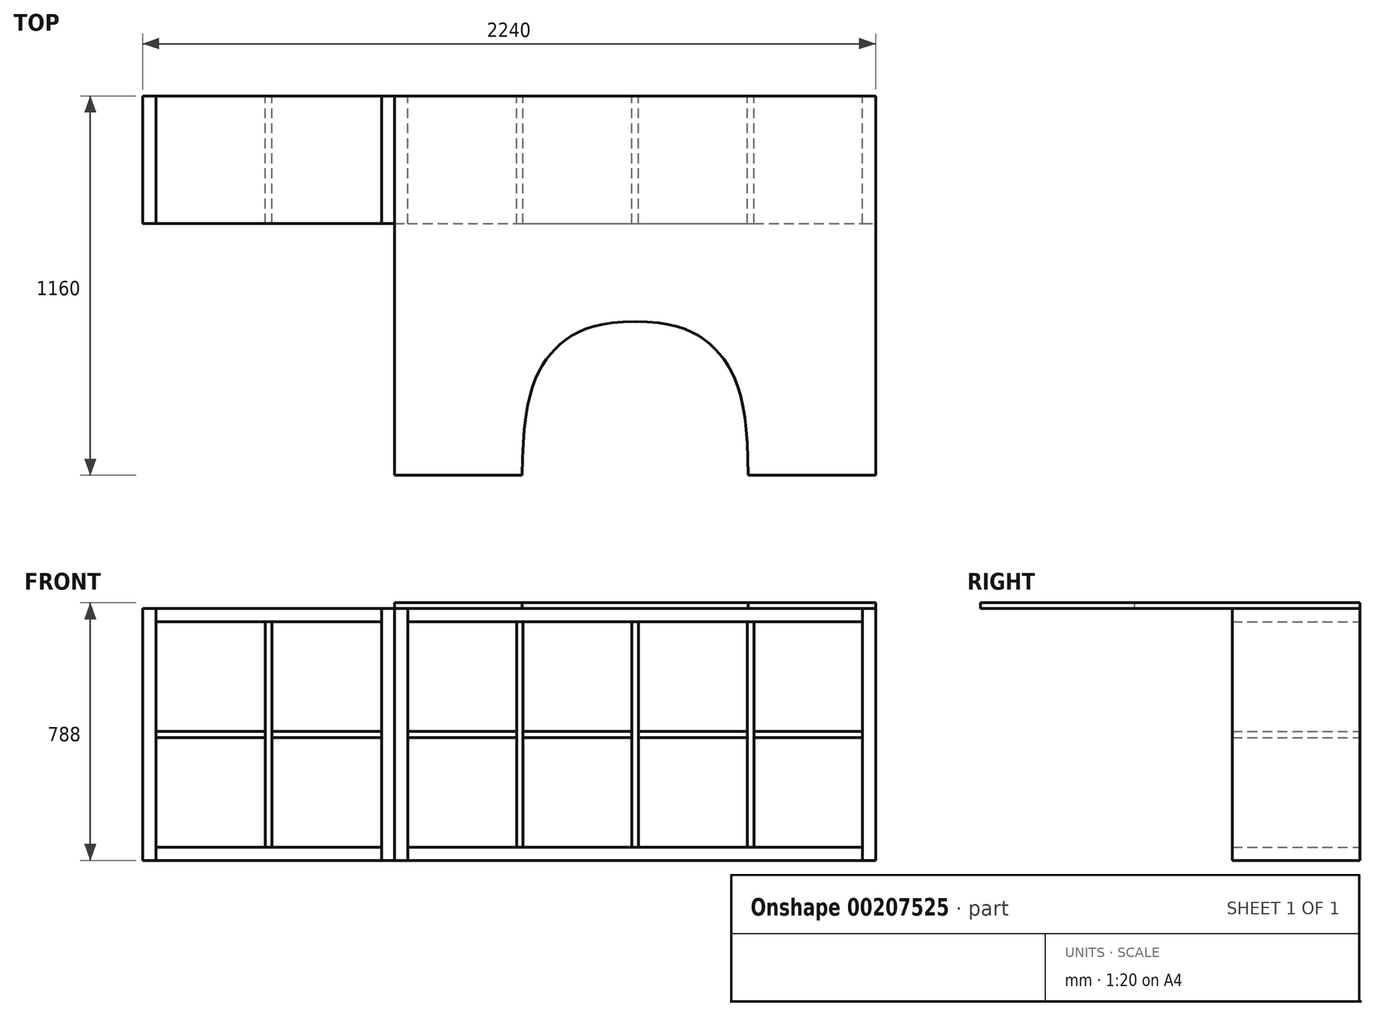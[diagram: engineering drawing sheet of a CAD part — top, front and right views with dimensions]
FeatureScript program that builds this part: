
annotation { "Feature Type Name" : "Feature", "Feature Type Description" : "" }
export const myFeature = defineFeature(function(context is Context, id is Id, definition is map)
    precondition{}
    {
        {
            var Q0;
            Q0=qCreatedBy(makeId("Front.planeOp"),FACE);
            var sketch = newSketch(context, id + "F0", { "sketchPlane" : qUnion([Q0])});
            skLineSegment(sketch, "E0.bottom", {"start": v(0, 0) * mm, "end": v(-770, 0) * mm});
            skLineSegment(sketch, "E0.top", {"start": v(0, 770) * mm, "end": v(-770, 770) * mm});
            skLineSegment(sketch, "E0.left", {"start": v(0, 0) * mm, "end": v(0, 770) * mm});
            skLineSegment(sketch, "E0.right", {"start": v(-770, 0) * mm, "end": v(-770, 770) * mm});
            skLineSegment(sketch, "E1", {"start": v(-770, 385) * mm, "end": v(0, 385) * mm, "construction": true});
            skLineSegment(sketch, "E2", {"start": v(-385, 770) * mm, "end": v(-385, 0) * mm, "construction": true});
            skLineSegment(sketch, "E3", {"start": v(-730, 395) * mm, "end": v(-395, 395) * mm});
            skLineSegment(sketch, "E4", {"start": v(-395, 730) * mm, "end": v(-395, 40) * mm});
            skLineSegment(sketch, "E5.MirrorCS", {"start": v(-375, 730) * mm, "end": v(-375, 40) * mm});
            skLineSegment(sketch, "E6.MirrorCS", {"start": v(-730, 375) * mm, "end": v(-395, 375) * mm});
            skLineSegment(sketch, "E7", {"start": v(-730, 770) * mm, "end": v(-730, 0) * mm});
            skLineSegment(sketch, "E8.MirrorCS", {"start": v(-40, 770) * mm, "end": v(-40, 0) * mm});
            skLineSegment(sketch, "E9", {"start": v(-730, 730) * mm, "end": v(-40, 730) * mm});
            skLineSegment(sketch, "E10.MirrorCS", {"start": v(-730, 40) * mm, "end": v(-40, 40) * mm});
            skPoint(sketch, "E11.orphan", {"position": v(-395, 770) * mm});
            skPoint(sketch, "E12.orphan", {"position": v(-375, 770) * mm});
            skPoint(sketch, "E13.orphan", {"position": v(-770, 395) * mm});
            skPoint(sketch, "E14.orphan", {"position": v(-770, 375) * mm});
            skPoint(sketch, "E15.orphan", {"position": v(0, 395) * mm});
            skPoint(sketch, "E16.orphan", {"position": v(0, 375) * mm});
            skLineSegment(sketch, "E17.trimOffspring", {"start": v(-375, 395) * mm, "end": v(-40, 395) * mm});
            skLineSegment(sketch, "E18.trimOffspring", {"start": v(-375, 375) * mm, "end": v(-40, 375) * mm});
            skPoint(sketch, "E19.orphan", {"position": v(-395, 0) * mm});
            skPoint(sketch, "E20.orphan", {"position": v(-375, 0) * mm});
            skLineSegment(sketch, "E21.bottom", {"start": v(0, 0) * mm, "end": v(1470, 0) * mm});
            skLineSegment(sketch, "E21.top", {"start": v(0, 770) * mm, "end": v(1470, 770) * mm});
            skLineSegment(sketch, "E21.right", {"start": v(1470, 0) * mm, "end": v(1470, 770) * mm});
            skLineSegment(sketch, "E22", {"start": v(0, 385) * mm, "end": v(1470, 385) * mm, "construction": true});
            skLineSegment(sketch, "E23", {"start": v(735, 770) * mm, "end": v(735, 0) * mm, "construction": true});
            skLineSegment(sketch, "E24.bottom", {"start": v(40, 730) * mm, "end": v(1430, 730) * mm});
            skLineSegment(sketch, "E24.top", {"start": v(40, 40) * mm, "end": v(1430, 40) * mm});
            skLineSegment(sketch, "E24.left", {"start": v(40, 770) * mm, "end": v(40, 0) * mm});
            skLineSegment(sketch, "E24.right", {"start": v(1430, 770) * mm, "end": v(1430, 0) * mm});
            skPoint(sketch, "E24.middle", {"position": v(735, 385) * mm});
            skLineSegment(sketch, "E25", {"start": v(725, 730) * mm, "end": v(725, 40) * mm});
            skLineSegment(sketch, "E26", {"start": v(40, 395) * mm, "end": v(372.5, 395) * mm});
            skLineSegment(sketch, "E27.MirrorCS", {"start": v(745, 730) * mm, "end": v(745, 40) * mm});
            skLineSegment(sketch, "E28.MirrorCS", {"start": v(40, 375) * mm, "end": v(372.5, 375) * mm});
            skLineSegment(sketch, "E29", {"start": v(382.5, 730) * mm, "end": v(382.5, 40) * mm, "construction": true});
            skLineSegment(sketch, "E30", {"start": v(372.5, 730) * mm, "end": v(372.5, 40) * mm});
            skLineSegment(sketch, "E31.MirrorCS", {"start": v(392.5, 730) * mm, "end": v(392.5, 40) * mm});
            skLineSegment(sketch, "E32.MirrorCS", {"start": v(1077.5, 730) * mm, "end": v(1077.5, 40) * mm});
            skLineSegment(sketch, "E33.MirrorCS", {"start": v(1097.5, 730) * mm, "end": v(1097.5, 40) * mm});
            skLineSegment(sketch, "E34.trimOffspring", {"start": v(1097.5, 375) * mm, "end": v(1430, 375) * mm});
            skLineSegment(sketch, "E35.trimOffspring", {"start": v(1097.5, 395) * mm, "end": v(1430, 395) * mm});
            skLineSegment(sketch, "E36.trimOffspring", {"start": v(745, 375) * mm, "end": v(1077.5, 375) * mm});
            skLineSegment(sketch, "E37.trimOffspring", {"start": v(745, 395) * mm, "end": v(1077.5, 395) * mm});
            skLineSegment(sketch, "E38.trimOffspring", {"start": v(392.5, 375) * mm, "end": v(725, 375) * mm});
            skLineSegment(sketch, "E39.trimOffspring", {"start": v(392.5, 395) * mm, "end": v(725, 395) * mm});
            skSolve(sketch);
        }
        {
            var Q0;
            {var subQ4=sQuery(id+"F0.wireOp",EDGE,"E0.right");Q0=makeQuery(id+"F0.imprint","IMPRINT",FACE,{"disambiguationData":[TD([[makeQuery(id+"F0.imprint","IMPRINT",EDGE,{"derivedFrom":subQ4}),-1.0]])]});}
            var Q1;
            {var subQ5=sQuery(id+"F0.wireOp",EDGE,"E4");var subQ8=makeQuery(id+"F0.imprint","INTERSECT",VERTEX,{"derivedFrom":[sQuery(id+"F0.wireOp",EDGE,"E3"),subQ5]});Q1=makeQuery(id+"F0.imprint","IMPRINT",FACE,{"disambiguationData":[TD([[makeQuery(id+"F0.imprint","IMPRINT",EDGE,{"disambiguationData":[TD([[subQ8,1.0]])],"derivedFrom":subQ5}),1.0]])]});}
            var Q2;
            {var subQ5=sQuery(id+"F0.wireOp",EDGE,"E0.left");Q2=makeQuery(id+"F0.imprint","IMPRINT",FACE,{"disambiguationData":[TD([[makeQuery(id+"F0.imprint","IMPRINT",EDGE,{"derivedFrom":subQ5}),1.0]])]});}
            var Q3;
            {var subQ0=sQuery(id+"F0.wireOp",EDGE,"E30");var subQ7=sQuery(id+"F0.wireOp",EDGE,"E24.bottom");var subQ8=makeQuery(id+"F0.imprint","INTERSECT",VERTEX,{"derivedFrom":[subQ7,subQ0]});Q3=makeQuery(id+"F0.imprint","IMPRINT",FACE,{"disambiguationData":[TD([[makeQuery(id+"F0.imprint","IMPRINT",EDGE,{"disambiguationData":[TD([[subQ8,-1.0]])],"derivedFrom":subQ7}),-1.0]])]});}
            var Q4;
            {var subQ0=sQuery(id+"F0.wireOp",EDGE,"E25");var subQ3=sQuery(id+"F0.wireOp",EDGE,"E24.bottom");var subQ4=makeQuery(id+"F0.imprint","INTERSECT",VERTEX,{"derivedFrom":[subQ3,subQ0]});Q4=makeQuery(id+"F0.imprint","IMPRINT",FACE,{"disambiguationData":[TD([[makeQuery(id+"F0.imprint","IMPRINT",EDGE,{"disambiguationData":[TD([[subQ4,-1.0]])],"derivedFrom":subQ3}),-1.0]])]});}
            var Q5;
            {var subQ0=sQuery(id+"F0.wireOp",EDGE,"E32.MirrorCS");var subQ7=sQuery(id+"F0.wireOp",EDGE,"E24.bottom");var subQ8=makeQuery(id+"F0.imprint","INTERSECT",VERTEX,{"derivedFrom":[subQ7,subQ0]});Q5=makeQuery(id+"F0.imprint","IMPRINT",FACE,{"disambiguationData":[TD([[makeQuery(id+"F0.imprint","IMPRINT",EDGE,{"disambiguationData":[TD([[subQ8,-1.0]])],"derivedFrom":subQ7}),-1.0]])]});}
            var Q6;
            {var subQ4=sQuery(id+"F0.wireOp",EDGE,"E21.right");Q6=makeQuery(id+"F0.imprint","IMPRINT",FACE,{"disambiguationData":[TD([[makeQuery(id+"F0.imprint","IMPRINT",EDGE,{"derivedFrom":subQ4}),1.0]])]});}
            extrude(context, id + "F1", {"entities" : qUnion([Q0, Q1, Q2, Q3, Q4, Q5, Q6]), "depth" : 390 * mm});
        }
        {
            var Q0;
            {var subQ2=sQuery(id+"F0.wireOp",EDGE,"E7");var subQ4=sQuery(id+"F0.wireOp",EDGE,"E0.top");var subQ5=makeQuery(id+"F0.imprint","INTERSECT",VERTEX,{"derivedFrom":[subQ4,subQ2]});Q0=makeQuery(id+"F0.imprint","IMPRINT",FACE,{"disambiguationData":[TD([[makeQuery(id+"F0.imprint","IMPRINT",EDGE,{"disambiguationData":[TD([[subQ5,1.0]])],"derivedFrom":subQ4}),1.0]])]});}
            var Q1;
            {var subQ0=sQuery(id+"F0.wireOp",EDGE,"E3");Q1=makeQuery(id+"F0.imprint","IMPRINT",FACE,{"disambiguationData":[TD([[makeQuery(id+"F0.imprint","IMPRINT",EDGE,{"derivedFrom":subQ0}),-1.0]])]});}
            var Q2;
            {var subQ0=sQuery(id+"F0.wireOp",EDGE,"E17.trimOffspring");Q2=makeQuery(id+"F0.imprint","IMPRINT",FACE,{"disambiguationData":[TD([[makeQuery(id+"F0.imprint","IMPRINT",EDGE,{"derivedFrom":subQ0}),-1.0]])]});}
            var Q3;
            {var subQ2=sQuery(id+"F0.wireOp",EDGE,"E7");var subQ4=sQuery(id+"F0.wireOp",EDGE,"E0.bottom");var subQ5=makeQuery(id+"F0.imprint","INTERSECT",VERTEX,{"derivedFrom":[subQ4,subQ2]});Q3=makeQuery(id+"F0.imprint","IMPRINT",FACE,{"disambiguationData":[TD([[makeQuery(id+"F0.imprint","IMPRINT",EDGE,{"disambiguationData":[TD([[subQ5,1.0]])],"derivedFrom":subQ4}),-1.0]])]});}
            var Q4;
            {var subQ0=sQuery(id+"F0.wireOp",EDGE,"E0.left");Q4=makeQuery(id+"F0.imprint","IMPRINT",FACE,{"disambiguationData":[TD([[makeQuery(id+"F0.imprint","IMPRINT",EDGE,{"derivedFrom":subQ0}),-1.0]])]});}
            var Q5;
            {var subQ0=sQuery(id+"F0.wireOp",EDGE,"E38.trimOffspring");Q5=makeQuery(id+"F0.imprint","IMPRINT",FACE,{"disambiguationData":[TD([[makeQuery(id+"F0.imprint","IMPRINT",EDGE,{"derivedFrom":subQ0}),1.0]])]});}
            var Q6;
            {var subQ0=sQuery(id+"F0.wireOp",EDGE,"E36.trimOffspring");Q6=makeQuery(id+"F0.imprint","IMPRINT",FACE,{"disambiguationData":[TD([[makeQuery(id+"F0.imprint","IMPRINT",EDGE,{"derivedFrom":subQ0}),1.0]])]});}
            var Q7;
            {var subQ0=sQuery(id+"F0.wireOp",EDGE,"E34.trimOffspring");Q7=makeQuery(id+"F0.imprint","IMPRINT",FACE,{"disambiguationData":[TD([[makeQuery(id+"F0.imprint","IMPRINT",EDGE,{"derivedFrom":subQ0}),1.0]])]});}
            extrude(context, id + "F2", {"entities" : qUnion([Q0, Q1, Q2, Q3, Q4, Q5, Q6, Q7]), "depth" : 390 * mm});
        }
        {
            var Q0;
            {var subQ0=sQuery(id+"F0.wireOp",EDGE,"E24.left");var subQ6=sQuery(id+"F0.wireOp",EDGE,"E21.bottom");var subQ7=makeQuery(id+"F0.imprint","INTERSECT",VERTEX,{"derivedFrom":[subQ6,subQ0]});Q0=makeQuery(id+"F0.imprint","IMPRINT",FACE,{"disambiguationData":[TD([[makeQuery(id+"F0.imprint","IMPRINT",EDGE,{"disambiguationData":[TD([[subQ7,-1.0]])],"derivedFrom":subQ6}),1.0]])]});}
            var Q1;
            {var subQ0=sQuery(id+"F0.wireOp",EDGE,"E26");Q1=makeQuery(id+"F0.imprint","IMPRINT",FACE,{"disambiguationData":[TD([[makeQuery(id+"F0.imprint","IMPRINT",EDGE,{"derivedFrom":subQ0}),-1.0]])]});}
            var Q2;
            {var subQ4=sQuery(id+"F0.wireOp",EDGE,"E24.left");var subQ6=sQuery(id+"F0.wireOp",EDGE,"E21.top");var subQ7=makeQuery(id+"F0.imprint","INTERSECT",VERTEX,{"derivedFrom":[subQ6,subQ4]});Q2=makeQuery(id+"F0.imprint","IMPRINT",FACE,{"disambiguationData":[TD([[makeQuery(id+"F0.imprint","IMPRINT",EDGE,{"disambiguationData":[TD([[subQ7,-1.0]])],"derivedFrom":subQ6}),-1.0]])]});}
            extrude(context, id + "F3", {"entities" : qUnion([Q0, Q1, Q2]), "depth" : 390 * mm});
        }
        {
            var Q0;
            Q0=makeQuery(id+"F3.opExtrude","SWEPT_FACE",FACE,{"disambiguationData":[OSD([sQuery(id+"F0.wireOp",EDGE,"E21.top")])]});
            var sketch = newSketch(context, id + "F4", { "sketchPlane" : qUnion([Q0])});
            skLineSegment(sketch, "E40.0", {"start": v(0, 0) * mm, "end": v(1470, 0) * mm});
            skLineSegment(sketch, "E40.1", {"start": v(1470, -390) * mm, "end": v(1470, 0) * mm});
            skLineSegment(sketch, "E40.2", {"start": v(0, -390) * mm, "end": v(0, 0) * mm});
            skPoint(sketch, "E41.orphan", {"position": v(40, 0) * mm});
            skPoint(sketch, "E42.orphan", {"position": v(1430, 0) * mm});
            skLineSegment(sketch, "E43", {"start": v(0, -390) * mm, "end": v(0, -1160) * mm});
            skLineSegment(sketch, "E44", {"start": v(735, 0) * mm, "end": v(735, -1160) * mm, "construction": true});
            skLineSegment(sketch, "E45", {"start": v(390, 0) * mm, "end": v(390, -1160) * mm, "construction": true});
            skLineSegment(sketch, "E46", {"start": v(0, -1160) * mm, "end": v(390, -1160) * mm});
            skLineSegment(sketch, "E47", {"start": v(390, -690) * mm, "end": v(735, -690) * mm, "construction": true});
            skFitSpline(sketch, "E48", {"points": [v(390, -1160) * mm, v(485.7, -778.94) * mm, v(735, -690) * mm], "startDerivative": vector(0, 1244.1) * mm, "endDerivative": vector(893.4, 0) * mm});
            skFitSpline(sketch, "E49.MirrorCS", {"points": [v(1080, -1160) * mm, v(984.3, -778.94) * mm, v(735, -690) * mm], "startDerivative": vector(0, 1244.1) * mm, "endDerivative": vector(-893.4, 0) * mm});
            skLineSegment(sketch, "E50.MirrorCS", {"start": v(1470, -1160) * mm, "end": v(1080, -1160) * mm});
            skLineSegment(sketch, "E51.MirrorCS", {"start": v(1470, -390) * mm, "end": v(1470, -1160) * mm});
            skPoint(sketch, "E52", {"position": v(562.5, -690) * mm});
            skSolve(sketch);
        }
        {
            var Q0;
            {var subQ5=sQuery(id+"F4.wireOp",EDGE,"E40.1");Q0=makeQuery(id+"F4.imprint","IMPRINT",FACE,{"disambiguationData":[TD([[makeQuery(id+"F4.imprint","IMPRINT",EDGE,{"derivedFrom":subQ5}),1.0]])]});}
            var Q1;
            {var subQ1=sQuery(id+"F0.wireOp",EDGE,"E21.top");Q1=makeQuery(id+"F4.imprint","IMPRINT",FACE,{"disambiguationData":[TD([[makeQuery(id+"F4.imprint","IMPRINT",EDGE,{"derivedFrom":makeQuery(id+"F3.opExtrude","CAP_EDGE",EDGE,{"disambiguationData":[OSD([subQ1])],"isStart":false})}),1.0]])]});}
            extrude(context, id + "F5", {"entities" : qUnion([Q0, Q1]), "depth" : 18 * mm});
        }
    });
